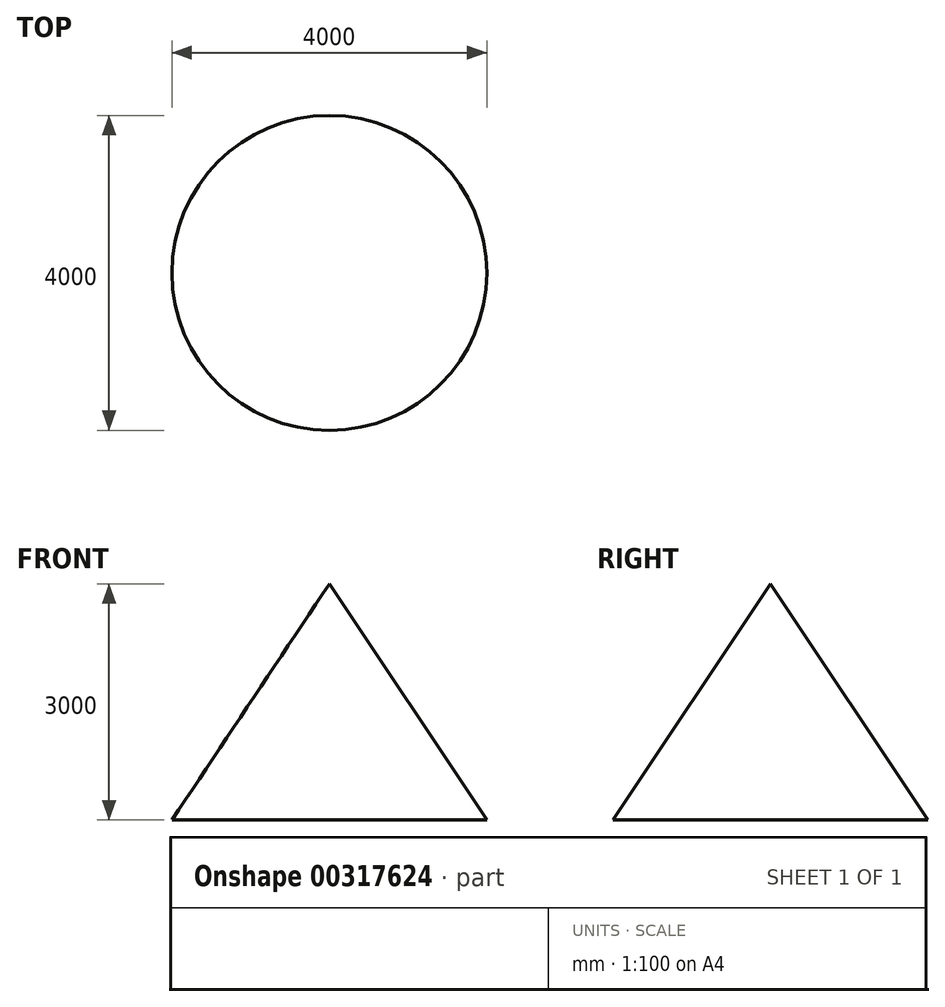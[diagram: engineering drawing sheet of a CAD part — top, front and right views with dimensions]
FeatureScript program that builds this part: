
annotation { "Feature Type Name" : "Feature", "Feature Type Description" : "" }
export const myFeature = defineFeature(function(context is Context, id is Id, definition is map)
    precondition{}
    {
        {
            var Q0;
            Q0=qCreatedBy(makeId("Right.planeOp"),FACE);
            var sketch = newSketch(context, id + "F0", { "sketchPlane" : qUnion([Q0])});
            skLineSegment(sketch, "E0", {"start": v(0, 0) * mm, "end": v(0, 3000) * mm});
            skLineSegment(sketch, "E1", {"start": v(0, 0) * mm, "end": v(-2000, 0) * mm});
            skLineSegment(sketch, "E2", {"start": v(0, 3000) * mm, "end": v(-2000, 0) * mm});
            skSolve(sketch);
        }
        {
            var Q0;
            Q0=makeQuery(id+"F0.imprint","IMPRINT",FACE,{"disambiguationData":[TD([[makeQuery(id+"F0.imprint","IMPRINT",EDGE,{"derivedFrom":sQuery(id+"F0.wireOp",EDGE,"E0")}),1.0]])]});
            var Q1;
            Q1=sQuery(id+"F0.wireOp",EDGE,"E0");
            revolve(context, id + "F1", {"entities" : qUnion([Q0]), "axis" : qUnion([Q1]), "revolveType" : RevolveType.FULL});
        }
    });
